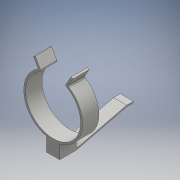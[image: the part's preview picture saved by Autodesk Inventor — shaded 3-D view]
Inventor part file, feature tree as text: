
AUTODESK INVENTOR PART (.ipt)
format: ipt  version: 2016 (Build 200138000, 138)  size: 153,088 bytes
history: native  units: mm
features: fillet x3, extrude x2, sketch x2
ambient origin geometry x8: Origin, YZ Plane, XZ Plane, XY Plane, X Axis, Y Axis, Z Axis, Center Point
bodies: Solide1 (feature_tree)
feature tree (7):
  extrude  "Extrusion1"  Depth=90.0mm
  extrude  "Extrusion2"  Depth=60.0mm
  fillet  "Congé1"  [1 undecoded]
  fillet  "Congé2"  Radius=60.0mm
  fillet  "Congé3"  [1 undecoded]
  sketch  "Esquisse1"
  sketch  "Esquisse2"
note: 2 required parameter values undecoded (feature->parameter linkage not recoverable at this tier; creation-order binding heuristic only, values carry confidence <= 0.55)
